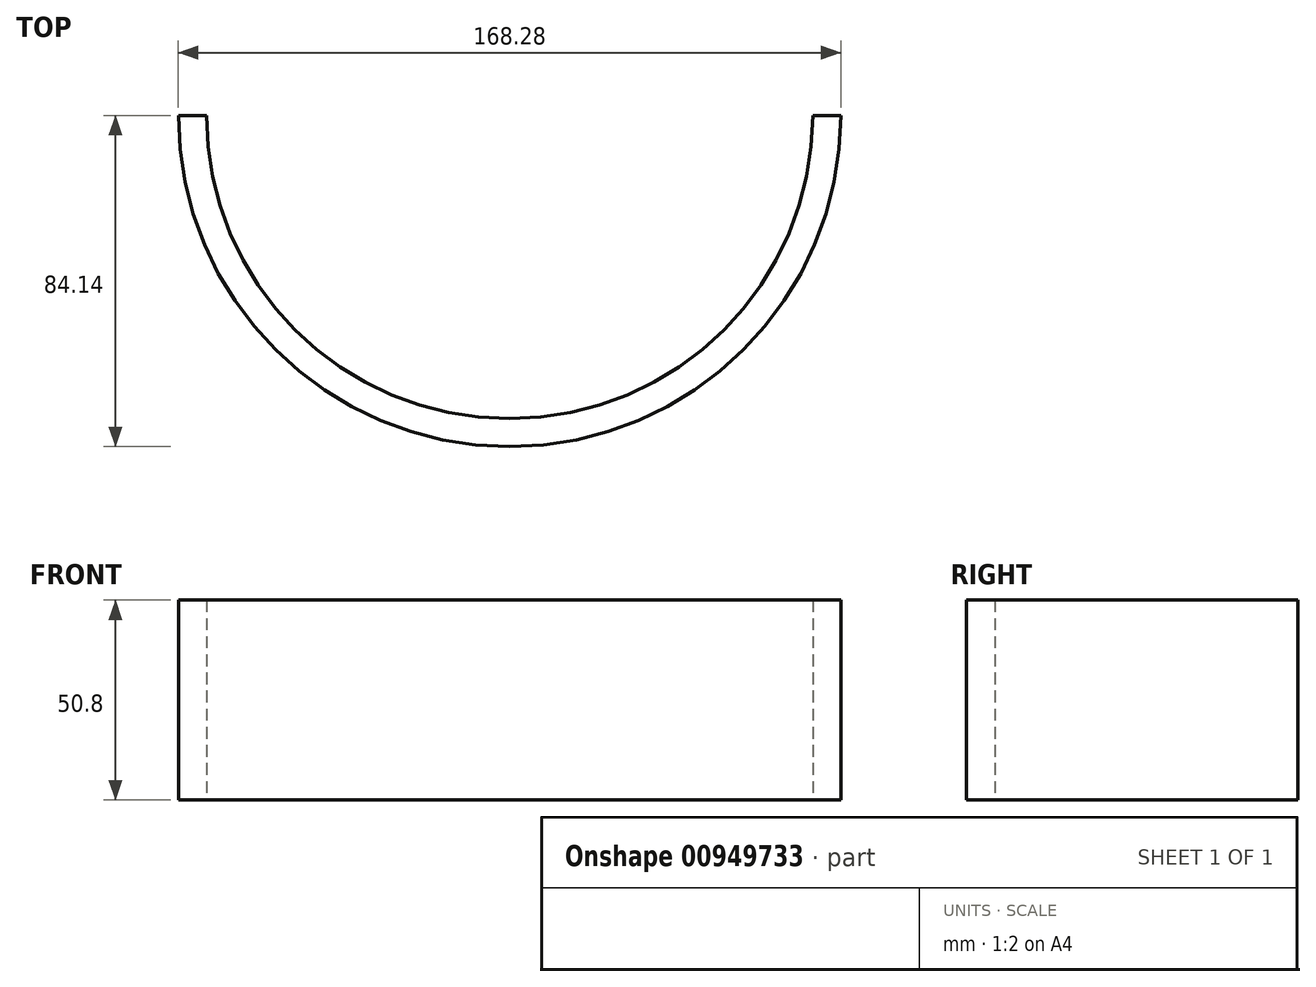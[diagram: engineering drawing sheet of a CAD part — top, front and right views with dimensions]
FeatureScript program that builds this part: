
annotation { "Feature Type Name" : "Feature", "Feature Type Description" : "" }
export const myFeature = defineFeature(function(context is Context, id is Id, definition is map)
    precondition{}
    {
        {
            var Q0;
            Q0=qCreatedBy(makeId("Top.planeOp"),FACE);
            var sketch = newSketch(context, id + "F0", { "sketchPlane" : qUnion([Q0])});
            skArc(sketch, "E0", {"start": v(-84.14, 0) * mm, "mid": v(0, -84.14) * mm, "end": v(84.14, 0) * mm});
            skArc(sketch, "E1", {"start": v(-77.03, 0) * mm, "mid": v(0, -77.03) * mm, "end": v(77.03, 0) * mm});
            skLineSegment(sketch, "E2", {"start": v(-84.14, 0) * mm, "end": v(-77.03, 0) * mm});
            skLineSegment(sketch, "E3", {"start": v(77.03, 0) * mm, "end": v(84.14, 0) * mm});
            skSolve(sketch);
        }
        {
            var Q0;
            Q0 = qSketchRegion(id + "F0", true);
            extrude(context, id + "F1", {"entities" : qUnion([Q0]), "endBound" : BoundingType.SYMMETRIC, "depth" : 50.8 * mm, "offsetDistance" : 25.4 * mm});
        }
    });
